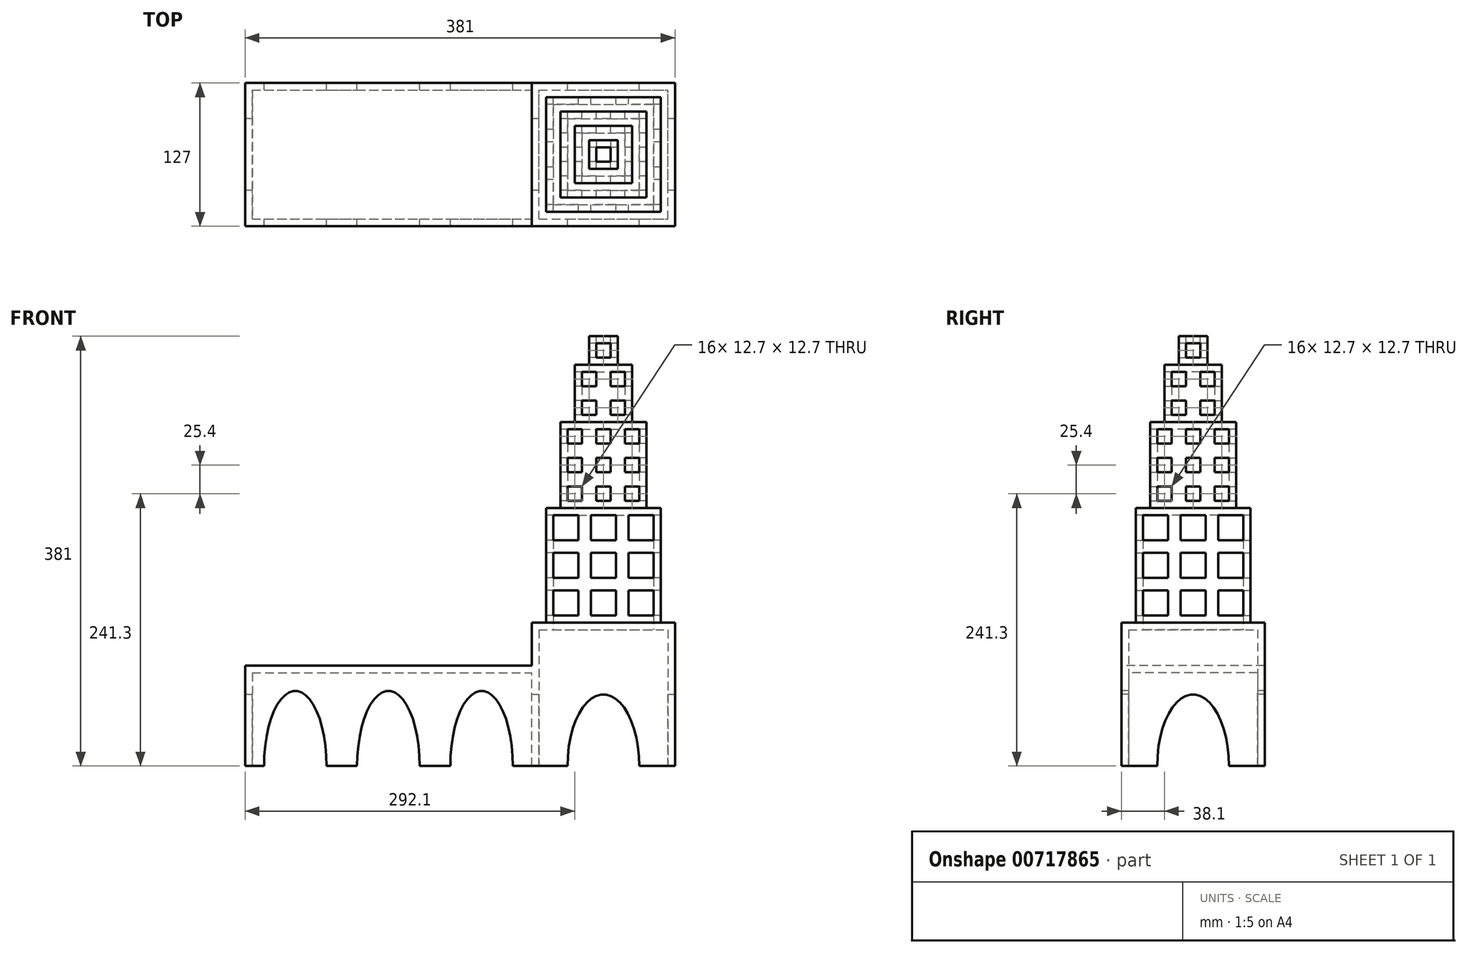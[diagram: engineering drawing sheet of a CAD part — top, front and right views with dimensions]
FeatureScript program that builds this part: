
annotation { "Feature Type Name" : "Feature", "Feature Type Description" : "" }
export const myFeature = defineFeature(function(context is Context, id is Id, definition is map)
    precondition{}
    {
        {
            var Q0;
            Q0=qCreatedBy(makeId("Front.planeOp"),FACE);
            var sketch = newSketch(context, id + "F0", { "sketchPlane" : qUnion([Q0])});
            skLineSegment(sketch, "E0.bottom", {"start": v(-63.5, 63.5) * mm, "end": v(63.5, 63.5) * mm});
            skLineSegment(sketch, "E0.top", {"start": v(-63.5, -63.5) * mm, "end": v(63.5, -63.5) * mm});
            skLineSegment(sketch, "E0.left", {"start": v(-63.5, 63.5) * mm, "end": v(-63.5, -63.5) * mm});
            skLineSegment(sketch, "E0.right", {"start": v(63.5, 63.5) * mm, "end": v(63.5, -63.5) * mm});
            skPoint(sketch, "E0.middle", {"position": v(0, 0) * mm});
            skSolve(sketch);
        }
        {
            var Q0;
            Q0 = qSketchRegion(id + "F0", true);
            extrude(context, id + "F1", {"entities" : qUnion([Q0]), "endBound" : BoundingType.SYMMETRIC, "depth" : 127 * mm, "offsetDistance" : 25.4 * mm});
        }
        {
            var Q0;
            Q0=makeQuery(id+"F1.opExtrude","SWEPT_FACE",FACE,{"disambiguationData":[OSD([sQuery(id+"F0.wireOp",EDGE,"E0.bottom")])]});
            var sketch = newSketch(context, id + "F2", { "sketchPlane" : qUnion([Q0])});
            skLineSegment(sketch, "E1.bottom", {"start": v(-50.8, 50.8) * mm, "end": v(50.8, 50.8) * mm});
            skLineSegment(sketch, "E1.top", {"start": v(-50.8, -50.8) * mm, "end": v(50.8, -50.8) * mm});
            skLineSegment(sketch, "E1.left", {"start": v(-50.8, 50.8) * mm, "end": v(-50.8, -50.8) * mm});
            skLineSegment(sketch, "E1.right", {"start": v(50.8, 50.8) * mm, "end": v(50.8, -50.8) * mm});
            skPoint(sketch, "E1.middle", {"position": v(0, 0) * mm});
            skSolve(sketch);
        }
        {
            var Q0;
            Q0 = qSketchRegion(id + "F2", true);
            extrude(context, id + "F3", {"entities" : qUnion([Q0]), "operationType" : NewBodyOperationType.ADD, "depth" : 101.6 * mm, "offsetDistance" : 25.4 * mm});
        }
        {
            var Q0;
            Q0=makeQuery(id+"F3.opExtrude","CAP_FACE",FACE,{"disambiguationData":[OSD([sQuery(id+"F2.wireOp",EDGE,"E1.bottom"),sQuery(id+"F2.wireOp",EDGE,"E1.top"),sQuery(id+"F2.wireOp",EDGE,"E1.left"),sQuery(id+"F2.wireOp",EDGE,"E1.right")])],"isStart":false});
            var sketch = newSketch(context, id + "F4", { "sketchPlane" : qUnion([Q0])});
            skLineSegment(sketch, "E2.bottom", {"start": v(-38.1, 38.1) * mm, "end": v(38.1, 38.1) * mm});
            skLineSegment(sketch, "E2.top", {"start": v(-38.1, -38.1) * mm, "end": v(38.1, -38.1) * mm});
            skLineSegment(sketch, "E2.left", {"start": v(-38.1, 38.1) * mm, "end": v(-38.1, -38.1) * mm});
            skLineSegment(sketch, "E2.right", {"start": v(38.1, 38.1) * mm, "end": v(38.1, -38.1) * mm});
            skPoint(sketch, "E2.middle", {"position": v(0, 0) * mm});
            skSolve(sketch);
        }
        {
            var Q0;
            Q0 = qSketchRegion(id + "F4", true);
            extrude(context, id + "F5", {"entities" : qUnion([Q0]), "operationType" : NewBodyOperationType.ADD, "depth" : 76.2 * mm, "offsetDistance" : 25.4 * mm});
        }
        {
            var Q0;
            Q0=makeQuery(id+"F5.opExtrude","CAP_FACE",FACE,{"disambiguationData":[OSD([sQuery(id+"F4.wireOp",EDGE,"E2.bottom"),sQuery(id+"F4.wireOp",EDGE,"E2.top"),sQuery(id+"F4.wireOp",EDGE,"E2.left"),sQuery(id+"F4.wireOp",EDGE,"E2.right")])],"isStart":false});
            var sketch = newSketch(context, id + "F6", { "sketchPlane" : qUnion([Q0])});
            skLineSegment(sketch, "E3.bottom", {"start": v(-25.4, 25.4) * mm, "end": v(25.4, 25.4) * mm});
            skLineSegment(sketch, "E3.top", {"start": v(-25.4, -25.4) * mm, "end": v(25.4, -25.4) * mm});
            skLineSegment(sketch, "E3.left", {"start": v(-25.4, 25.4) * mm, "end": v(-25.4, -25.4) * mm});
            skLineSegment(sketch, "E3.right", {"start": v(25.4, 25.4) * mm, "end": v(25.4, -25.4) * mm});
            skPoint(sketch, "E3.middle", {"position": v(0, 0) * mm});
            skSolve(sketch);
        }
        {
            var Q0;
            Q0 = qSketchRegion(id + "F6", true);
            extrude(context, id + "F7", {"entities" : qUnion([Q0]), "operationType" : NewBodyOperationType.ADD, "depth" : 50.8 * mm, "offsetDistance" : 25.4 * mm});
        }
        {
            var Q0;
            Q0=makeQuery(id+"F7.opExtrude","CAP_FACE",FACE,{"disambiguationData":[OSD([sQuery(id+"F6.wireOp",EDGE,"E3.bottom"),sQuery(id+"F6.wireOp",EDGE,"E3.top"),sQuery(id+"F6.wireOp",EDGE,"E3.left"),sQuery(id+"F6.wireOp",EDGE,"E3.right")])],"isStart":false});
            var sketch = newSketch(context, id + "F8", { "sketchPlane" : qUnion([Q0])});
            skLineSegment(sketch, "E4.bottom", {"start": v(-12.7, 12.7) * mm, "end": v(12.7, 12.7) * mm});
            skLineSegment(sketch, "E4.top", {"start": v(-12.7, -12.7) * mm, "end": v(12.7, -12.7) * mm});
            skLineSegment(sketch, "E4.left", {"start": v(-12.7, 12.7) * mm, "end": v(-12.7, -12.7) * mm});
            skLineSegment(sketch, "E4.right", {"start": v(12.7, 12.7) * mm, "end": v(12.7, -12.7) * mm});
            skPoint(sketch, "E4.middle", {"position": v(0, 0) * mm});
            skSolve(sketch);
        }
        {
            var Q0;
            Q0 = qSketchRegion(id + "F8", true);
            extrude(context, id + "F9", {"entities" : qUnion([Q0]), "operationType" : NewBodyOperationType.ADD, "depth" : 25.4 * mm, "offsetDistance" : 25.4 * mm});
        }
        {
            var Q0;
            Q0=makeQuery(id+"F1.opExtrude","SWEPT_FACE",FACE,{"disambiguationData":[OSD([sQuery(id+"F0.wireOp",EDGE,"E0.top")])]});
            shell(context, id + "F10", {"entities" : qUnion([Q0]), "thickness" : 6.35 * mm});
        }
        {
            var Q0;
            Q0=makeQuery(id+"F1.opExtrude","SWEPT_FACE",FACE,{"disambiguationData":[OSD([sQuery(id+"F0.wireOp",EDGE,"E0.left")])]});
            var sketch = newSketch(context, id + "F11", { "sketchPlane" : qUnion([Q0])});
            skLineSegment(sketch, "E5", {"start": v(63.5, -63.5) * mm, "end": v(-63.5, -63.5) * mm});
            skLineSegment(sketch, "E6", {"start": v(-63.5, -63.5) * mm, "end": v(-63.5, 25.4) * mm});
            skLineSegment(sketch, "E7", {"start": v(63.5, -63.5) * mm, "end": v(63.5, 25.4) * mm});
            skLineSegment(sketch, "E8", {"start": v(-63.5, 25.4) * mm, "end": v(63.5, 25.4) * mm});
            skSolve(sketch);
        }
        {
            var Q0;
            Q0 = qSketchRegion(id + "F11", true);
            extrude(context, id + "F12", {"entities" : qUnion([Q0]), "operationType" : NewBodyOperationType.ADD, "depth" : 254 * mm, "offsetDistance" : 25.4 * mm});
        }
        {
            var Q0;
            Q0=makeQuery(id+"F12.opExtrude","CAP_FACE",FACE,{"disambiguationData":[OSD([sQuery(id+"F11.wireOp",EDGE,"E5"),sQuery(id+"F11.wireOp",EDGE,"E6"),sQuery(id+"F11.wireOp",EDGE,"E7"),sQuery(id+"F11.wireOp",EDGE,"E8")])],"isStart":false});
            var sketch = newSketch(context, id + "F13", { "sketchPlane" : qUnion([Q0])});
            skEllipse(sketch, "E9", {"center": v(0, -63.5) * mm, "majorRadius": 63.5 * mm, "minorRadius": 31.75 * mm, "majorAxis": v(0, 1)});
            skSolve(sketch);
        }
        {
            var Q0;
            Q0=makeQuery(id+"F12.boolean.opBoolean","MERGE",FACE,{"derivedFrom":[makeQuery(id+"F1.opExtrude","SWEPT_FACE",FACE,{"disambiguationData":[OSD([sQuery(id+"F0.wireOp",EDGE,"E0.top")])]}),makeQuery(id+"F12.opExtrude","SWEPT_FACE",FACE,{"disambiguationData":[OSD([sQuery(id+"F11.wireOp",EDGE,"E5")])]})]});
            shell(context, id + "F14", {"entities" : qUnion([Q0]), "thickness" : 6.35 * mm});
        }
        {
            var Q0;
            Q0 = qSketchRegion(id + "F13", true);
            extrude(context, id + "F15", {"entities" : qUnion([Q0]), "operationType" : NewBodyOperationType.REMOVE, "endBound" : BoundingType.THROUGH_ALL, "oppositeDirection" : true, "depth" : 270 * mm, "offsetDistance" : 25.4 * mm});
        }
        {
            var Q0;
            Q0=makeQuery(id+"F12.boolean.opBoolean","MERGE",FACE,{"derivedFrom":[makeQuery(id+"F1.opExtrude","CAP_FACE",FACE,{"disambiguationData":[OSD([sQuery(id+"F0.wireOp",EDGE,"E0.bottom"),sQuery(id+"F0.wireOp",EDGE,"E0.top"),sQuery(id+"F0.wireOp",EDGE,"E0.left"),sQuery(id+"F0.wireOp",EDGE,"E0.right")])],"isStart":true}),makeQuery(id+"F12.opExtrude","SWEPT_FACE",FACE,{"disambiguationData":[OSD([sQuery(id+"F11.wireOp",EDGE,"E6")])]})]});
            var sketch = newSketch(context, id + "F16", { "sketchPlane" : qUnion([Q0])});
            skLineSegment(sketch, "E10", {"start": v(162.78, -63.5) * mm, "end": v(218.22, -63.5) * mm});
            skLineSegment(sketch, "E11", {"start": v(317.5, 3.18) * mm, "end": v(317.5, 25.4) * mm});
            skEllipticalArc(sketch, "E12", {});
            skPoint(sketch, "E13", {"position": v(190.5, 3.18) * mm});
            skPoint(sketch, "E14", {"position": v(190.5, 3.17) * mm});
            skPoint(sketch, "E15.orphan", {"position": v(63.5, -63.5) * mm});
            skPoint(sketch, "E16.orphan", {"position": v(317.5, -63.5) * mm});
            skEllipticalArc(sketch, "E17.1.0.0", {});
            skLineSegment(sketch, "E17.1.0.1", {"start": v(245.33, -63.5) * mm, "end": v(300.77, -63.5) * mm});
            skEllipticalArc(sketch, "E18.1.0.0", {});
            skLineSegment(sketch, "E19", {"start": v(80.23, -63.5) * mm, "end": v(135.67, -63.5) * mm});
            const initialGuessF16  = {"E12": [0.1905, -0.0635, 0, 1, 0.066675, 0.027722105175231253, 4.71238898038469, 1.5707963267948966], "E17.1.0.0": [0.27305, -0.0635, 0, 1, 0.066675, 0.027722105175231253, 4.71238898038469, 1.5707963267948966], "E18.1.0.0": [0.10795, -0.0635, 0, 1, 0.066675, 0.027722105175231253, 4.71238898038469, 1.5707963267948966]};
            skSetInitialGuess(sketch, initialGuessF16);
            skSolve(sketch);
        }
        {
            var Q0;
            Q0 = qSketchRegion(id + "F16", true);
            extrude(context, id + "F17", {"entities" : qUnion([Q0]), "operationType" : NewBodyOperationType.REMOVE, "oppositeDirection" : true, "depth" : 127 * mm, "offsetDistance" : 25.4 * mm});
        }
        {
            var Q0;
            Q0=makeQuery(id+"F3.opExtrude","SWEPT_FACE",FACE,{"disambiguationData":[OSD([sQuery(id+"F2.wireOp",EDGE,"E1.bottom")])]});
            var sketch = newSketch(context, id + "F18", { "sketchPlane" : qUnion([Q0])});
            skLineSegment(sketch, "E20.2", {"start": v(44.45, 158.75) * mm, "end": v(22.22, 158.75) * mm});
            skLineSegment(sketch, "E20.3", {"start": v(44.45, 136.53) * mm, "end": v(44.45, 158.75) * mm});
            skPoint(sketch, "E21.orphan", {"position": v(-44.45, 114.3) * mm});
            skPoint(sketch, "E22.orphan", {"position": v(0, 69.85) * mm});
            skPoint(sketch, "E23.orphan", {"position": v(44.45, 69.85) * mm});
            skPoint(sketch, "E24.orphan", {"position": v(-44.45, 69.85) * mm});
            skPoint(sketch, "E20.1.start.orphan", {"position": v(-44.45, 158.75) * mm});
            skLineSegment(sketch, "E25", {"start": v(22.22, 136.53) * mm, "end": v(44.45, 136.53) * mm});
            skLineSegment(sketch, "E26", {"start": v(22.22, 136.53) * mm, "end": v(22.22, 158.75) * mm});
            skPoint(sketch, "E27.orphan", {"position": v(0, 158.75) * mm});
            skPoint(sketch, "E28.start.orphan", {"position": v(0, 136.53) * mm});
            skPoint(sketch, "E29.start.orphan", {"position": v(0, 114.3) * mm});
            skPoint(sketch, "E30.orphan", {"position": v(44.45, 114.3) * mm});
            skLineSegment(sketch, "E31.0.1.0", {"start": v(22.22, 103.19) * mm, "end": v(22.22, 125.41) * mm});
            skLineSegment(sketch, "E31.0.1.1", {"start": v(44.45, 125.41) * mm, "end": v(22.22, 125.41) * mm});
            skLineSegment(sketch, "E31.0.1.2", {"start": v(44.45, 103.19) * mm, "end": v(44.45, 125.41) * mm});
            skLineSegment(sketch, "E31.0.1.3", {"start": v(22.22, 103.19) * mm, "end": v(44.45, 103.19) * mm});
            skLineSegment(sketch, "E31.0.2.0", {"start": v(22.22, 69.85) * mm, "end": v(22.22, 92.08) * mm});
            skLineSegment(sketch, "E31.0.2.1", {"start": v(44.45, 92.08) * mm, "end": v(22.22, 92.08) * mm});
            skLineSegment(sketch, "E31.0.2.2", {"start": v(44.45, 69.85) * mm, "end": v(44.45, 92.08) * mm});
            skLineSegment(sketch, "E31.0.2.3", {"start": v(22.22, 69.85) * mm, "end": v(44.45, 69.85) * mm});
            skLineSegment(sketch, "E31.1.0.0", {"start": v(-11.11, 136.53) * mm, "end": v(-11.11, 158.75) * mm});
            skLineSegment(sketch, "E31.1.0.1", {"start": v(11.11, 158.75) * mm, "end": v(-11.11, 158.75) * mm});
            skLineSegment(sketch, "E31.1.0.2", {"start": v(11.11, 136.53) * mm, "end": v(11.11, 158.75) * mm});
            skLineSegment(sketch, "E31.1.0.3", {"start": v(-11.11, 136.53) * mm, "end": v(11.11, 136.53) * mm});
            skLineSegment(sketch, "E31.1.1.0", {"start": v(-11.11, 103.19) * mm, "end": v(-11.11, 125.41) * mm});
            skLineSegment(sketch, "E31.1.1.1", {"start": v(11.11, 125.41) * mm, "end": v(-11.11, 125.41) * mm});
            skLineSegment(sketch, "E31.1.1.2", {"start": v(11.11, 103.19) * mm, "end": v(11.11, 125.41) * mm});
            skLineSegment(sketch, "E31.1.1.3", {"start": v(-11.11, 103.19) * mm, "end": v(11.11, 103.19) * mm});
            skLineSegment(sketch, "E31.1.2.0", {"start": v(-11.11, 69.85) * mm, "end": v(-11.11, 92.08) * mm});
            skLineSegment(sketch, "E31.1.2.1", {"start": v(11.11, 92.08) * mm, "end": v(-11.11, 92.08) * mm});
            skLineSegment(sketch, "E31.1.2.2", {"start": v(11.11, 69.85) * mm, "end": v(11.11, 92.08) * mm});
            skLineSegment(sketch, "E31.1.2.3", {"start": v(-11.11, 69.85) * mm, "end": v(11.11, 69.85) * mm});
            skLineSegment(sketch, "E31.2.0.0", {"start": v(-44.45, 136.53) * mm, "end": v(-44.45, 158.75) * mm});
            skLineSegment(sketch, "E31.2.0.1", {"start": v(-22.23, 158.75) * mm, "end": v(-44.45, 158.75) * mm});
            skLineSegment(sketch, "E31.2.0.2", {"start": v(-22.23, 136.53) * mm, "end": v(-22.23, 158.75) * mm});
            skLineSegment(sketch, "E31.2.0.3", {"start": v(-44.45, 136.53) * mm, "end": v(-22.23, 136.53) * mm});
            skLineSegment(sketch, "E31.2.1.0", {"start": v(-44.45, 103.19) * mm, "end": v(-44.45, 125.41) * mm});
            skLineSegment(sketch, "E31.2.1.1", {"start": v(-22.23, 125.41) * mm, "end": v(-44.45, 125.41) * mm});
            skLineSegment(sketch, "E31.2.1.2", {"start": v(-22.23, 103.19) * mm, "end": v(-22.23, 125.41) * mm});
            skLineSegment(sketch, "E31.2.1.3", {"start": v(-44.45, 103.19) * mm, "end": v(-22.23, 103.19) * mm});
            skLineSegment(sketch, "E31.2.2.0", {"start": v(-44.45, 69.85) * mm, "end": v(-44.45, 92.08) * mm});
            skLineSegment(sketch, "E31.2.2.1", {"start": v(-22.23, 92.08) * mm, "end": v(-44.45, 92.08) * mm});
            skLineSegment(sketch, "E31.2.2.2", {"start": v(-22.23, 69.85) * mm, "end": v(-22.23, 92.08) * mm});
            skLineSegment(sketch, "E31.2.2.3", {"start": v(-44.45, 69.85) * mm, "end": v(-22.23, 69.85) * mm});
            skLineSegment(sketch, "E31.direction1", {"start": v(22.22, 136.53) * mm, "end": v(-11.11, 136.53) * mm, "construction": true});
            skLineSegment(sketch, "E31.direction2", {"start": v(22.22, 136.53) * mm, "end": v(22.22, 103.19) * mm, "construction": true});
            skSolve(sketch);
        }
        {
            var Q0;
            Q0=makeQuery(id+"F18.imprint","IMPRINT",FACE,{"disambiguationData":[TD([[makeQuery(id+"F18.imprint","IMPRINT",EDGE,{"derivedFrom":sQuery(id+"F18.wireOp",EDGE,"E31.2.0.0")}),-1.0]])]});
            var Q1;
            Q1=makeQuery(id+"F18.imprint","IMPRINT",FACE,{"disambiguationData":[TD([[makeQuery(id+"F18.imprint","IMPRINT",EDGE,{"derivedFrom":sQuery(id+"F18.wireOp",EDGE,"E31.1.0.0")}),-1.0]])]});
            var Q2;
            Q2=makeQuery(id+"F18.imprint","IMPRINT",FACE,{"disambiguationData":[TD([[makeQuery(id+"F18.imprint","IMPRINT",EDGE,{"derivedFrom":sQuery(id+"F18.wireOp",EDGE,"E20.2")}),1.0]])]});
            var Q3;
            Q3=makeQuery(id+"F18.imprint","IMPRINT",FACE,{"disambiguationData":[TD([[makeQuery(id+"F18.imprint","IMPRINT",EDGE,{"derivedFrom":sQuery(id+"F18.wireOp",EDGE,"E31.0.1.0")}),-1.0]])]});
            var Q4;
            Q4=makeQuery(id+"F18.imprint","IMPRINT",FACE,{"disambiguationData":[TD([[makeQuery(id+"F18.imprint","IMPRINT",EDGE,{"derivedFrom":sQuery(id+"F18.wireOp",EDGE,"E31.1.1.0")}),-1.0]])]});
            var Q5;
            Q5=makeQuery(id+"F18.imprint","IMPRINT",FACE,{"disambiguationData":[TD([[makeQuery(id+"F18.imprint","IMPRINT",EDGE,{"derivedFrom":sQuery(id+"F18.wireOp",EDGE,"E31.2.1.0")}),-1.0]])]});
            var Q6;
            Q6=makeQuery(id+"F18.imprint","IMPRINT",FACE,{"disambiguationData":[TD([[makeQuery(id+"F18.imprint","IMPRINT",EDGE,{"derivedFrom":sQuery(id+"F18.wireOp",EDGE,"E31.2.2.0")}),-1.0]])]});
            var Q7;
            Q7=makeQuery(id+"F18.imprint","IMPRINT",FACE,{"disambiguationData":[TD([[makeQuery(id+"F18.imprint","IMPRINT",EDGE,{"derivedFrom":sQuery(id+"F18.wireOp",EDGE,"E31.1.2.0")}),-1.0]])]});
            var Q8;
            Q8=makeQuery(id+"F18.imprint","IMPRINT",FACE,{"disambiguationData":[TD([[makeQuery(id+"F18.imprint","IMPRINT",EDGE,{"derivedFrom":sQuery(id+"F18.wireOp",EDGE,"E31.0.2.0")}),-1.0]])]});
            extrude(context, id + "F19", {"entities" : qUnion([Q0, Q1, Q2, Q3, Q4, Q5, Q6, Q7, Q8]), "operationType" : NewBodyOperationType.REMOVE, "endBound" : BoundingType.THROUGH_ALL, "oppositeDirection" : true, "depth" : 25.4 * mm, "offsetDistance" : 25.4 * mm});
        }
        {
            var Q0;
            Q0=makeQuery(id+"F3.opExtrude","SWEPT_FACE",FACE,{"disambiguationData":[OSD([sQuery(id+"F2.wireOp",EDGE,"E1.left")])]});
            var sketch = newSketch(context, id + "F20", { "sketchPlane" : qUnion([Q0])});
            skLineSegment(sketch, "E32.bottom", {"start": v(22.22, 158.75) * mm, "end": v(44.45, 158.75) * mm});
            skLineSegment(sketch, "E32.top", {"start": v(22.22, 136.53) * mm, "end": v(44.45, 136.53) * mm});
            skLineSegment(sketch, "E32.left", {"start": v(22.22, 158.75) * mm, "end": v(22.22, 136.53) * mm});
            skLineSegment(sketch, "E32.right", {"start": v(44.45, 158.75) * mm, "end": v(44.45, 136.53) * mm});
            skPoint(sketch, "E32.middle", {"position": v(33.34, 147.64) * mm});
            skLineSegment(sketch, "E33.0.1.0", {"start": v(22.22, 125.41) * mm, "end": v(22.22, 103.19) * mm});
            skLineSegment(sketch, "E33.0.1.1", {"start": v(22.22, 103.19) * mm, "end": v(44.45, 103.19) * mm});
            skLineSegment(sketch, "E33.0.1.2", {"start": v(44.45, 125.41) * mm, "end": v(44.45, 103.19) * mm});
            skLineSegment(sketch, "E33.0.1.3", {"start": v(22.22, 125.41) * mm, "end": v(44.45, 125.41) * mm});
            skLineSegment(sketch, "E33.0.2.0", {"start": v(22.22, 92.08) * mm, "end": v(22.22, 69.85) * mm});
            skLineSegment(sketch, "E33.0.2.1", {"start": v(22.22, 69.85) * mm, "end": v(44.45, 69.85) * mm});
            skLineSegment(sketch, "E33.0.2.2", {"start": v(44.45, 92.08) * mm, "end": v(44.45, 69.85) * mm});
            skLineSegment(sketch, "E33.0.2.3", {"start": v(22.22, 92.08) * mm, "end": v(44.45, 92.08) * mm});
            skLineSegment(sketch, "E33.1.0.0", {"start": v(-11.11, 158.75) * mm, "end": v(-11.11, 136.53) * mm});
            skLineSegment(sketch, "E33.1.0.1", {"start": v(-11.11, 136.53) * mm, "end": v(11.11, 136.53) * mm});
            skLineSegment(sketch, "E33.1.0.2", {"start": v(11.11, 158.75) * mm, "end": v(11.11, 136.53) * mm});
            skLineSegment(sketch, "E33.1.0.3", {"start": v(-11.11, 158.75) * mm, "end": v(11.11, 158.75) * mm});
            skLineSegment(sketch, "E33.1.1.0", {"start": v(-11.11, 125.41) * mm, "end": v(-11.11, 103.19) * mm});
            skLineSegment(sketch, "E33.1.1.1", {"start": v(-11.11, 103.19) * mm, "end": v(11.11, 103.19) * mm});
            skLineSegment(sketch, "E33.1.1.2", {"start": v(11.11, 125.41) * mm, "end": v(11.11, 103.19) * mm});
            skLineSegment(sketch, "E33.1.1.3", {"start": v(-11.11, 125.41) * mm, "end": v(11.11, 125.41) * mm});
            skLineSegment(sketch, "E33.1.2.0", {"start": v(-11.11, 92.08) * mm, "end": v(-11.11, 69.85) * mm});
            skLineSegment(sketch, "E33.1.2.1", {"start": v(-11.11, 69.85) * mm, "end": v(11.11, 69.85) * mm});
            skLineSegment(sketch, "E33.1.2.2", {"start": v(11.11, 92.08) * mm, "end": v(11.11, 69.85) * mm});
            skLineSegment(sketch, "E33.1.2.3", {"start": v(-11.11, 92.08) * mm, "end": v(11.11, 92.08) * mm});
            skLineSegment(sketch, "E33.2.0.0", {"start": v(-44.45, 158.75) * mm, "end": v(-44.45, 136.53) * mm});
            skLineSegment(sketch, "E33.2.0.1", {"start": v(-44.45, 136.53) * mm, "end": v(-22.23, 136.53) * mm});
            skLineSegment(sketch, "E33.2.0.2", {"start": v(-22.23, 158.75) * mm, "end": v(-22.23, 136.53) * mm});
            skLineSegment(sketch, "E33.2.0.3", {"start": v(-44.45, 158.75) * mm, "end": v(-22.23, 158.75) * mm});
            skLineSegment(sketch, "E33.2.1.0", {"start": v(-44.45, 125.41) * mm, "end": v(-44.45, 103.19) * mm});
            skLineSegment(sketch, "E33.2.1.1", {"start": v(-44.45, 103.19) * mm, "end": v(-22.23, 103.19) * mm});
            skLineSegment(sketch, "E33.2.1.2", {"start": v(-22.23, 125.41) * mm, "end": v(-22.23, 103.19) * mm});
            skLineSegment(sketch, "E33.2.1.3", {"start": v(-44.45, 125.41) * mm, "end": v(-22.23, 125.41) * mm});
            skLineSegment(sketch, "E33.2.2.0", {"start": v(-44.45, 92.08) * mm, "end": v(-44.45, 69.85) * mm});
            skLineSegment(sketch, "E33.2.2.1", {"start": v(-44.45, 69.85) * mm, "end": v(-22.23, 69.85) * mm});
            skLineSegment(sketch, "E33.2.2.2", {"start": v(-22.23, 92.08) * mm, "end": v(-22.23, 69.85) * mm});
            skLineSegment(sketch, "E33.2.2.3", {"start": v(-44.45, 92.08) * mm, "end": v(-22.23, 92.08) * mm});
            skLineSegment(sketch, "E33.direction1", {"start": v(22.22, 136.53) * mm, "end": v(-11.11, 136.53) * mm, "construction": true});
            skLineSegment(sketch, "E33.direction2", {"start": v(22.22, 136.53) * mm, "end": v(22.22, 103.19) * mm, "construction": true});
            skSolve(sketch);
        }
        {
            var Q0;
            Q0=makeQuery(id+"F20.imprint","IMPRINT",FACE,{"disambiguationData":[TD([[makeQuery(id+"F20.imprint","IMPRINT",EDGE,{"derivedFrom":sQuery(id+"F20.wireOp",EDGE,"E33.2.0.0")}),1.0]])]});
            var Q1;
            Q1=makeQuery(id+"F20.imprint","IMPRINT",FACE,{"disambiguationData":[TD([[makeQuery(id+"F20.imprint","IMPRINT",EDGE,{"derivedFrom":sQuery(id+"F20.wireOp",EDGE,"E33.1.0.0")}),1.0]])]});
            var Q2;
            Q2=makeQuery(id+"F20.imprint","IMPRINT",FACE,{"disambiguationData":[TD([[makeQuery(id+"F20.imprint","IMPRINT",EDGE,{"derivedFrom":sQuery(id+"F20.wireOp",EDGE,"E32.bottom")}),-1.0]])]});
            var Q3;
            Q3=makeQuery(id+"F20.imprint","IMPRINT",FACE,{"disambiguationData":[TD([[makeQuery(id+"F20.imprint","IMPRINT",EDGE,{"derivedFrom":sQuery(id+"F20.wireOp",EDGE,"E33.2.1.0")}),1.0]])]});
            var Q4;
            Q4=makeQuery(id+"F20.imprint","IMPRINT",FACE,{"disambiguationData":[TD([[makeQuery(id+"F20.imprint","IMPRINT",EDGE,{"derivedFrom":sQuery(id+"F20.wireOp",EDGE,"E33.1.1.0")}),1.0]])]});
            var Q5;
            Q5=makeQuery(id+"F20.imprint","IMPRINT",FACE,{"disambiguationData":[TD([[makeQuery(id+"F20.imprint","IMPRINT",EDGE,{"derivedFrom":sQuery(id+"F20.wireOp",EDGE,"E33.0.1.0")}),1.0]])]});
            var Q6;
            Q6=makeQuery(id+"F20.imprint","IMPRINT",FACE,{"disambiguationData":[TD([[makeQuery(id+"F20.imprint","IMPRINT",EDGE,{"derivedFrom":sQuery(id+"F20.wireOp",EDGE,"E33.2.2.0")}),1.0]])]});
            var Q7;
            Q7=makeQuery(id+"F20.imprint","IMPRINT",FACE,{"disambiguationData":[TD([[makeQuery(id+"F20.imprint","IMPRINT",EDGE,{"derivedFrom":sQuery(id+"F20.wireOp",EDGE,"E33.1.2.0")}),1.0]])]});
            var Q8;
            Q8=makeQuery(id+"F20.imprint","IMPRINT",FACE,{"disambiguationData":[TD([[makeQuery(id+"F20.imprint","IMPRINT",EDGE,{"derivedFrom":sQuery(id+"F20.wireOp",EDGE,"E33.0.2.0")}),1.0]])]});
            extrude(context, id + "F21", {"entities" : qUnion([Q0, Q1, Q2, Q3, Q4, Q5, Q6, Q7, Q8]), "operationType" : NewBodyOperationType.REMOVE, "endBound" : BoundingType.THROUGH_ALL, "oppositeDirection" : true, "depth" : 25.4 * mm, "offsetDistance" : 25.4 * mm});
        }
        {
            var Q0;
            Q0=makeQuery(id+"F9.opExtrude","SWEPT_FACE",FACE,{"disambiguationData":[OSD([sQuery(id+"F8.wireOp",EDGE,"E4.bottom")])]});
            var sketch = newSketch(context, id + "F22", { "sketchPlane" : qUnion([Q0])});
            skLineSegment(sketch, "E34.0", {"start": v(6.35, 311.15) * mm, "end": v(-6.35, 311.15) * mm});
            skLineSegment(sketch, "E34.1", {"start": v(6.35, 311.15) * mm, "end": v(6.35, 298.45) * mm});
            skLineSegment(sketch, "E34.2", {"start": v(6.35, 298.45) * mm, "end": v(-6.35, 298.45) * mm});
            skLineSegment(sketch, "E34.3", {"start": v(-6.35, 311.15) * mm, "end": v(-6.35, 298.45) * mm});
            skSolve(sketch);
        }
        {
            var Q0;
            Q0=makeQuery(id+"F22.imprint","IMPRINT",FACE,{"disambiguationData":[TD([[makeQuery(id+"F22.imprint","IMPRINT",EDGE,{"derivedFrom":sQuery(id+"F22.wireOp",EDGE,"E34.0")}),1.0]])]});
            extrude(context, id + "F23", {"entities" : qUnion([Q0]), "operationType" : NewBodyOperationType.REMOVE, "endBound" : BoundingType.THROUGH_ALL, "oppositeDirection" : true, "depth" : 25.4 * mm, "offsetDistance" : 25.4 * mm});
        }
        {
            var Q0;
            Q0=makeQuery(id+"F9.opExtrude","SWEPT_FACE",FACE,{"disambiguationData":[OSD([sQuery(id+"F8.wireOp",EDGE,"E4.left")])]});
            var sketch = newSketch(context, id + "F24", { "sketchPlane" : qUnion([Q0])});
            skLineSegment(sketch, "E35.0", {"start": v(-6.35, 311.15) * mm, "end": v(-6.35, 298.45) * mm});
            skLineSegment(sketch, "E35.1", {"start": v(-6.35, 311.15) * mm, "end": v(6.35, 311.15) * mm});
            skLineSegment(sketch, "E35.2", {"start": v(6.35, 311.15) * mm, "end": v(6.35, 298.45) * mm});
            skLineSegment(sketch, "E35.3", {"start": v(-6.35, 298.45) * mm, "end": v(6.35, 298.45) * mm});
            skSolve(sketch);
        }
        {
            var Q0;
            Q0=makeQuery(id+"F24.imprint","IMPRINT",FACE,{"disambiguationData":[TD([[makeQuery(id+"F24.imprint","IMPRINT",EDGE,{"derivedFrom":sQuery(id+"F24.wireOp",EDGE,"E35.0")}),1.0]])]});
            extrude(context, id + "F25", {"entities" : qUnion([Q0]), "operationType" : NewBodyOperationType.REMOVE, "endBound" : BoundingType.THROUGH_ALL, "oppositeDirection" : true, "depth" : 25.4 * mm, "offsetDistance" : 25.4 * mm});
        }
        {
            var Q0;
            Q0=makeQuery(id+"F12.boolean.opBoolean","MERGE",FACE,{"derivedFrom":[makeQuery(id+"F1.opExtrude","CAP_FACE",FACE,{"disambiguationData":[OSD([sQuery(id+"F0.wireOp",EDGE,"E0.bottom"),sQuery(id+"F0.wireOp",EDGE,"E0.top"),sQuery(id+"F0.wireOp",EDGE,"E0.left"),sQuery(id+"F0.wireOp",EDGE,"E0.right")])],"isStart":true}),makeQuery(id+"F12.opExtrude","SWEPT_FACE",FACE,{"disambiguationData":[OSD([sQuery(id+"F11.wireOp",EDGE,"E6")])]})]});
            var sketch = newSketch(context, id + "F26", { "sketchPlane" : qUnion([Q0])});
            skEllipse(sketch, "E36", {"center": v(0, -63.5) * mm, "majorRadius": 63.5 * mm, "minorRadius": 31.75 * mm, "majorAxis": v(0, 1)});
            skSolve(sketch);
        }
        {
            var Q0;
            Q0 = qSketchRegion(id + "F26", true);
            extrude(context, id + "F27", {"entities" : qUnion([Q0]), "operationType" : NewBodyOperationType.REMOVE, "endBound" : BoundingType.THROUGH_ALL, "oppositeDirection" : true, "depth" : 25.4 * mm, "offsetDistance" : 25.4 * mm});
        }
        {
            var Q0;
            Q0=makeQuery(id+"F5.opExtrude","SWEPT_FACE",FACE,{"disambiguationData":[OSD([sQuery(id+"F4.wireOp",EDGE,"E2.bottom")])]});
            var sketch = newSketch(context, id + "F28", { "sketchPlane" : qUnion([Q0])});
            skLineSegment(sketch, "E37.bottom", {"start": v(19.05, 234.95) * mm, "end": v(31.75, 234.95) * mm});
            skLineSegment(sketch, "E37.top", {"start": v(19.05, 222.25) * mm, "end": v(31.75, 222.25) * mm});
            skLineSegment(sketch, "E37.left", {"start": v(19.05, 234.95) * mm, "end": v(19.05, 222.25) * mm});
            skLineSegment(sketch, "E37.right", {"start": v(31.75, 234.95) * mm, "end": v(31.75, 222.25) * mm});
            skPoint(sketch, "E37.middle", {"position": v(25.4, 228.6) * mm});
            skLineSegment(sketch, "E38.0.1.0", {"start": v(19.05, 209.55) * mm, "end": v(31.75, 209.55) * mm});
            skLineSegment(sketch, "E38.0.1.1", {"start": v(19.05, 209.55) * mm, "end": v(19.05, 196.85) * mm});
            skLineSegment(sketch, "E38.0.1.2", {"start": v(19.05, 196.85) * mm, "end": v(31.75, 196.85) * mm});
            skLineSegment(sketch, "E38.0.1.3", {"start": v(31.75, 209.55) * mm, "end": v(31.75, 196.85) * mm});
            skLineSegment(sketch, "E38.0.2.0", {"start": v(19.05, 184.15) * mm, "end": v(31.75, 184.15) * mm});
            skLineSegment(sketch, "E38.0.2.1", {"start": v(19.05, 184.15) * mm, "end": v(19.05, 171.45) * mm});
            skLineSegment(sketch, "E38.0.2.2", {"start": v(19.05, 171.45) * mm, "end": v(31.75, 171.45) * mm});
            skLineSegment(sketch, "E38.0.2.3", {"start": v(31.75, 184.15) * mm, "end": v(31.75, 171.45) * mm});
            skLineSegment(sketch, "E38.1.0.0", {"start": v(-6.35, 234.95) * mm, "end": v(6.35, 234.95) * mm});
            skLineSegment(sketch, "E38.1.0.1", {"start": v(-6.35, 234.95) * mm, "end": v(-6.35, 222.25) * mm});
            skLineSegment(sketch, "E38.1.0.2", {"start": v(-6.35, 222.25) * mm, "end": v(6.35, 222.25) * mm});
            skLineSegment(sketch, "E38.1.0.3", {"start": v(6.35, 234.95) * mm, "end": v(6.35, 222.25) * mm});
            skLineSegment(sketch, "E38.1.1.0", {"start": v(-6.35, 209.55) * mm, "end": v(6.35, 209.55) * mm});
            skLineSegment(sketch, "E38.1.1.1", {"start": v(-6.35, 209.55) * mm, "end": v(-6.35, 196.85) * mm});
            skLineSegment(sketch, "E38.1.1.2", {"start": v(-6.35, 196.85) * mm, "end": v(6.35, 196.85) * mm});
            skLineSegment(sketch, "E38.1.1.3", {"start": v(6.35, 209.55) * mm, "end": v(6.35, 196.85) * mm});
            skLineSegment(sketch, "E38.1.2.0", {"start": v(-6.35, 184.15) * mm, "end": v(6.35, 184.15) * mm});
            skLineSegment(sketch, "E38.1.2.1", {"start": v(-6.35, 184.15) * mm, "end": v(-6.35, 171.45) * mm});
            skLineSegment(sketch, "E38.1.2.2", {"start": v(-6.35, 171.45) * mm, "end": v(6.35, 171.45) * mm});
            skLineSegment(sketch, "E38.1.2.3", {"start": v(6.35, 184.15) * mm, "end": v(6.35, 171.45) * mm});
            skLineSegment(sketch, "E38.2.0.0", {"start": v(-31.75, 234.95) * mm, "end": v(-19.05, 234.95) * mm});
            skLineSegment(sketch, "E38.2.0.1", {"start": v(-31.75, 234.95) * mm, "end": v(-31.75, 222.25) * mm});
            skLineSegment(sketch, "E38.2.0.2", {"start": v(-31.75, 222.25) * mm, "end": v(-19.05, 222.25) * mm});
            skLineSegment(sketch, "E38.2.0.3", {"start": v(-19.05, 234.95) * mm, "end": v(-19.05, 222.25) * mm});
            skLineSegment(sketch, "E38.2.1.0", {"start": v(-31.75, 209.55) * mm, "end": v(-19.05, 209.55) * mm});
            skLineSegment(sketch, "E38.2.1.1", {"start": v(-31.75, 209.55) * mm, "end": v(-31.75, 196.85) * mm});
            skLineSegment(sketch, "E38.2.1.2", {"start": v(-31.75, 196.85) * mm, "end": v(-19.05, 196.85) * mm});
            skLineSegment(sketch, "E38.2.1.3", {"start": v(-19.05, 209.55) * mm, "end": v(-19.05, 196.85) * mm});
            skLineSegment(sketch, "E38.2.2.0", {"start": v(-31.75, 184.15) * mm, "end": v(-19.05, 184.15) * mm});
            skLineSegment(sketch, "E38.2.2.1", {"start": v(-31.75, 184.15) * mm, "end": v(-31.75, 171.45) * mm});
            skLineSegment(sketch, "E38.2.2.2", {"start": v(-31.75, 171.45) * mm, "end": v(-19.05, 171.45) * mm});
            skLineSegment(sketch, "E38.2.2.3", {"start": v(-19.05, 184.15) * mm, "end": v(-19.05, 171.45) * mm});
            skLineSegment(sketch, "E38.direction1", {"start": v(19.05, 234.95) * mm, "end": v(-6.35, 234.95) * mm, "construction": true});
            skLineSegment(sketch, "E38.direction2", {"start": v(19.05, 234.95) * mm, "end": v(19.05, 209.55) * mm, "construction": true});
            skSolve(sketch);
        }
        {
            var Q0;
            Q0=makeQuery(id+"F28.imprint","IMPRINT",FACE,{"disambiguationData":[TD([[makeQuery(id+"F28.imprint","IMPRINT",EDGE,{"derivedFrom":sQuery(id+"F28.wireOp",EDGE,"E38.2.0.0")}),-1.0]])]});
            var Q1;
            Q1=makeQuery(id+"F28.imprint","IMPRINT",FACE,{"disambiguationData":[TD([[makeQuery(id+"F28.imprint","IMPRINT",EDGE,{"derivedFrom":sQuery(id+"F28.wireOp",EDGE,"E38.2.1.0")}),-1.0]])]});
            var Q2;
            Q2=makeQuery(id+"F28.imprint","IMPRINT",FACE,{"disambiguationData":[TD([[makeQuery(id+"F28.imprint","IMPRINT",EDGE,{"derivedFrom":sQuery(id+"F28.wireOp",EDGE,"E38.2.2.0")}),-1.0]])]});
            var Q3;
            Q3=makeQuery(id+"F28.imprint","IMPRINT",FACE,{"disambiguationData":[TD([[makeQuery(id+"F28.imprint","IMPRINT",EDGE,{"derivedFrom":sQuery(id+"F28.wireOp",EDGE,"E38.1.2.0")}),-1.0]])]});
            var Q4;
            Q4=makeQuery(id+"F28.imprint","IMPRINT",FACE,{"disambiguationData":[TD([[makeQuery(id+"F28.imprint","IMPRINT",EDGE,{"derivedFrom":sQuery(id+"F28.wireOp",EDGE,"E38.1.1.0")}),-1.0]])]});
            var Q5;
            Q5=makeQuery(id+"F28.imprint","IMPRINT",FACE,{"disambiguationData":[TD([[makeQuery(id+"F28.imprint","IMPRINT",EDGE,{"derivedFrom":sQuery(id+"F28.wireOp",EDGE,"E38.1.0.0")}),-1.0]])]});
            var Q6;
            Q6=makeQuery(id+"F28.imprint","IMPRINT",FACE,{"disambiguationData":[TD([[makeQuery(id+"F28.imprint","IMPRINT",EDGE,{"derivedFrom":sQuery(id+"F28.wireOp",EDGE,"E37.bottom")}),-1.0]])]});
            var Q7;
            Q7=makeQuery(id+"F28.imprint","IMPRINT",FACE,{"disambiguationData":[TD([[makeQuery(id+"F28.imprint","IMPRINT",EDGE,{"derivedFrom":sQuery(id+"F28.wireOp",EDGE,"E38.0.1.0")}),-1.0]])]});
            var Q8;
            Q8=makeQuery(id+"F28.imprint","IMPRINT",FACE,{"disambiguationData":[TD([[makeQuery(id+"F28.imprint","IMPRINT",EDGE,{"derivedFrom":sQuery(id+"F28.wireOp",EDGE,"E38.0.2.0")}),-1.0]])]});
            extrude(context, id + "F29", {"entities" : qUnion([Q0, Q1, Q2, Q3, Q4, Q5, Q6, Q7, Q8]), "operationType" : NewBodyOperationType.REMOVE, "endBound" : BoundingType.THROUGH_ALL, "oppositeDirection" : true, "depth" : 25.4 * mm, "offsetDistance" : 25.4 * mm});
        }
        {
            var Q0;
            Q0=makeQuery(id+"F5.opExtrude","SWEPT_FACE",FACE,{"disambiguationData":[OSD([sQuery(id+"F4.wireOp",EDGE,"E2.left")])]});
            var sketch = newSketch(context, id + "F30", { "sketchPlane" : qUnion([Q0])});
            skLineSegment(sketch, "E39.bottom", {"start": v(19.05, 234.95) * mm, "end": v(31.75, 234.95) * mm});
            skLineSegment(sketch, "E39.top", {"start": v(19.05, 222.25) * mm, "end": v(31.75, 222.25) * mm});
            skLineSegment(sketch, "E39.left", {"start": v(19.05, 234.95) * mm, "end": v(19.05, 222.25) * mm});
            skLineSegment(sketch, "E39.right", {"start": v(31.75, 234.95) * mm, "end": v(31.75, 222.25) * mm});
            skPoint(sketch, "E39.middle", {"position": v(25.4, 228.6) * mm});
            skLineSegment(sketch, "E40.0.1.0", {"start": v(19.05, 209.55) * mm, "end": v(31.75, 209.55) * mm});
            skLineSegment(sketch, "E40.0.1.1", {"start": v(19.05, 209.55) * mm, "end": v(19.05, 196.85) * mm});
            skLineSegment(sketch, "E40.0.1.2", {"start": v(19.05, 196.85) * mm, "end": v(31.75, 196.85) * mm});
            skLineSegment(sketch, "E40.0.1.3", {"start": v(31.75, 209.55) * mm, "end": v(31.75, 196.85) * mm});
            skLineSegment(sketch, "E40.0.2.0", {"start": v(19.05, 184.15) * mm, "end": v(31.75, 184.15) * mm});
            skLineSegment(sketch, "E40.0.2.1", {"start": v(19.05, 184.15) * mm, "end": v(19.05, 171.45) * mm});
            skLineSegment(sketch, "E40.0.2.2", {"start": v(19.05, 171.45) * mm, "end": v(31.75, 171.45) * mm});
            skLineSegment(sketch, "E40.0.2.3", {"start": v(31.75, 184.15) * mm, "end": v(31.75, 171.45) * mm});
            skLineSegment(sketch, "E40.1.0.0", {"start": v(-6.35, 234.95) * mm, "end": v(6.35, 234.95) * mm});
            skLineSegment(sketch, "E40.1.0.1", {"start": v(-6.35, 234.95) * mm, "end": v(-6.35, 222.25) * mm});
            skLineSegment(sketch, "E40.1.0.2", {"start": v(-6.35, 222.25) * mm, "end": v(6.35, 222.25) * mm});
            skLineSegment(sketch, "E40.1.0.3", {"start": v(6.35, 234.95) * mm, "end": v(6.35, 222.25) * mm});
            skLineSegment(sketch, "E40.1.1.0", {"start": v(-6.35, 209.55) * mm, "end": v(6.35, 209.55) * mm});
            skLineSegment(sketch, "E40.1.1.1", {"start": v(-6.35, 209.55) * mm, "end": v(-6.35, 196.85) * mm});
            skLineSegment(sketch, "E40.1.1.2", {"start": v(-6.35, 196.85) * mm, "end": v(6.35, 196.85) * mm});
            skLineSegment(sketch, "E40.1.1.3", {"start": v(6.35, 209.55) * mm, "end": v(6.35, 196.85) * mm});
            skLineSegment(sketch, "E40.1.2.0", {"start": v(-6.35, 184.15) * mm, "end": v(6.35, 184.15) * mm});
            skLineSegment(sketch, "E40.1.2.1", {"start": v(-6.35, 184.15) * mm, "end": v(-6.35, 171.45) * mm});
            skLineSegment(sketch, "E40.1.2.2", {"start": v(-6.35, 171.45) * mm, "end": v(6.35, 171.45) * mm});
            skLineSegment(sketch, "E40.1.2.3", {"start": v(6.35, 184.15) * mm, "end": v(6.35, 171.45) * mm});
            skLineSegment(sketch, "E40.2.0.0", {"start": v(-31.75, 234.95) * mm, "end": v(-19.05, 234.95) * mm});
            skLineSegment(sketch, "E40.2.0.1", {"start": v(-31.75, 234.95) * mm, "end": v(-31.75, 222.25) * mm});
            skLineSegment(sketch, "E40.2.0.2", {"start": v(-31.75, 222.25) * mm, "end": v(-19.05, 222.25) * mm});
            skLineSegment(sketch, "E40.2.0.3", {"start": v(-19.05, 234.95) * mm, "end": v(-19.05, 222.25) * mm});
            skLineSegment(sketch, "E40.2.1.0", {"start": v(-31.75, 209.55) * mm, "end": v(-19.05, 209.55) * mm});
            skLineSegment(sketch, "E40.2.1.1", {"start": v(-31.75, 209.55) * mm, "end": v(-31.75, 196.85) * mm});
            skLineSegment(sketch, "E40.2.1.2", {"start": v(-31.75, 196.85) * mm, "end": v(-19.05, 196.85) * mm});
            skLineSegment(sketch, "E40.2.1.3", {"start": v(-19.05, 209.55) * mm, "end": v(-19.05, 196.85) * mm});
            skLineSegment(sketch, "E40.2.2.0", {"start": v(-31.75, 184.15) * mm, "end": v(-19.05, 184.15) * mm});
            skLineSegment(sketch, "E40.2.2.1", {"start": v(-31.75, 184.15) * mm, "end": v(-31.75, 171.45) * mm});
            skLineSegment(sketch, "E40.2.2.2", {"start": v(-31.75, 171.45) * mm, "end": v(-19.05, 171.45) * mm});
            skLineSegment(sketch, "E40.2.2.3", {"start": v(-19.05, 184.15) * mm, "end": v(-19.05, 171.45) * mm});
            skLineSegment(sketch, "E40.direction1", {"start": v(19.05, 234.95) * mm, "end": v(-6.35, 234.95) * mm, "construction": true});
            skLineSegment(sketch, "E40.direction2", {"start": v(19.05, 234.95) * mm, "end": v(19.05, 209.55) * mm, "construction": true});
            skSolve(sketch);
        }
        {
            var Q0;
            Q0=makeQuery(id+"F30.imprint","IMPRINT",FACE,{"disambiguationData":[TD([[makeQuery(id+"F30.imprint","IMPRINT",EDGE,{"derivedFrom":sQuery(id+"F30.wireOp",EDGE,"E40.2.0.0")}),-1.0]])]});
            var Q1;
            Q1=makeQuery(id+"F30.imprint","IMPRINT",FACE,{"disambiguationData":[TD([[makeQuery(id+"F30.imprint","IMPRINT",EDGE,{"derivedFrom":sQuery(id+"F30.wireOp",EDGE,"E40.1.0.0")}),-1.0]])]});
            var Q2;
            Q2=makeQuery(id+"F30.imprint","IMPRINT",FACE,{"disambiguationData":[TD([[makeQuery(id+"F30.imprint","IMPRINT",EDGE,{"derivedFrom":sQuery(id+"F30.wireOp",EDGE,"E39.bottom")}),-1.0]])]});
            var Q3;
            Q3=makeQuery(id+"F30.imprint","IMPRINT",FACE,{"disambiguationData":[TD([[makeQuery(id+"F30.imprint","IMPRINT",EDGE,{"derivedFrom":sQuery(id+"F30.wireOp",EDGE,"E40.0.1.0")}),-1.0]])]});
            var Q4;
            Q4=makeQuery(id+"F30.imprint","IMPRINT",FACE,{"disambiguationData":[TD([[makeQuery(id+"F30.imprint","IMPRINT",EDGE,{"derivedFrom":sQuery(id+"F30.wireOp",EDGE,"E40.1.1.0")}),-1.0]])]});
            var Q5;
            Q5=makeQuery(id+"F30.imprint","IMPRINT",FACE,{"disambiguationData":[TD([[makeQuery(id+"F30.imprint","IMPRINT",EDGE,{"derivedFrom":sQuery(id+"F30.wireOp",EDGE,"E40.1.2.0")}),-1.0]])]});
            var Q6;
            Q6=makeQuery(id+"F30.imprint","IMPRINT",FACE,{"disambiguationData":[TD([[makeQuery(id+"F30.imprint","IMPRINT",EDGE,{"derivedFrom":sQuery(id+"F30.wireOp",EDGE,"E40.2.2.0")}),-1.0]])]});
            var Q7;
            Q7=makeQuery(id+"F30.imprint","IMPRINT",FACE,{"disambiguationData":[TD([[makeQuery(id+"F30.imprint","IMPRINT",EDGE,{"derivedFrom":sQuery(id+"F30.wireOp",EDGE,"E40.2.1.0")}),-1.0]])]});
            var Q8;
            Q8=makeQuery(id+"F30.imprint","IMPRINT",FACE,{"disambiguationData":[TD([[makeQuery(id+"F30.imprint","IMPRINT",EDGE,{"derivedFrom":sQuery(id+"F30.wireOp",EDGE,"E40.0.2.0")}),-1.0]])]});
            extrude(context, id + "F31", {"entities" : qUnion([Q0, Q1, Q2, Q3, Q4, Q5, Q6, Q7, Q8]), "operationType" : NewBodyOperationType.REMOVE, "endBound" : BoundingType.THROUGH_ALL, "oppositeDirection" : true, "depth" : 25.4 * mm, "offsetDistance" : 25.4 * mm});
        }
        {
            var Q0;
            Q0=makeQuery(id+"F7.opExtrude","SWEPT_FACE",FACE,{"disambiguationData":[OSD([sQuery(id+"F6.wireOp",EDGE,"E3.bottom")])]});
            var sketch = newSketch(context, id + "F32", { "sketchPlane" : qUnion([Q0])});
            skLineSegment(sketch, "E41.bottom", {"start": v(6.35, 285.75) * mm, "end": v(19.05, 285.75) * mm});
            skLineSegment(sketch, "E41.top", {"start": v(6.35, 273.05) * mm, "end": v(19.05, 273.05) * mm});
            skLineSegment(sketch, "E41.left", {"start": v(6.35, 285.75) * mm, "end": v(6.35, 273.05) * mm});
            skLineSegment(sketch, "E41.right", {"start": v(19.05, 285.75) * mm, "end": v(19.05, 273.05) * mm});
            skPoint(sketch, "E41.middle", {"position": v(12.7, 279.4) * mm});
            skLineSegment(sketch, "E42.0.1.0", {"start": v(6.35, 260.35) * mm, "end": v(19.05, 260.35) * mm});
            skLineSegment(sketch, "E42.0.1.1", {"start": v(6.35, 260.35) * mm, "end": v(6.35, 247.65) * mm});
            skLineSegment(sketch, "E42.0.1.2", {"start": v(6.35, 247.65) * mm, "end": v(19.05, 247.65) * mm});
            skLineSegment(sketch, "E42.0.1.3", {"start": v(19.05, 260.35) * mm, "end": v(19.05, 247.65) * mm});
            skLineSegment(sketch, "E42.1.0.0", {"start": v(-19.05, 285.75) * mm, "end": v(-6.35, 285.75) * mm});
            skLineSegment(sketch, "E42.1.0.1", {"start": v(-19.05, 285.75) * mm, "end": v(-19.05, 273.05) * mm});
            skLineSegment(sketch, "E42.1.0.2", {"start": v(-19.05, 273.05) * mm, "end": v(-6.35, 273.05) * mm});
            skLineSegment(sketch, "E42.1.0.3", {"start": v(-6.35, 285.75) * mm, "end": v(-6.35, 273.05) * mm});
            skLineSegment(sketch, "E42.1.1.0", {"start": v(-19.05, 260.35) * mm, "end": v(-6.35, 260.35) * mm});
            skLineSegment(sketch, "E42.1.1.1", {"start": v(-19.05, 260.35) * mm, "end": v(-19.05, 247.65) * mm});
            skLineSegment(sketch, "E42.1.1.2", {"start": v(-19.05, 247.65) * mm, "end": v(-6.35, 247.65) * mm});
            skLineSegment(sketch, "E42.1.1.3", {"start": v(-6.35, 260.35) * mm, "end": v(-6.35, 247.65) * mm});
            skLineSegment(sketch, "E42.direction1", {"start": v(6.35, 285.75) * mm, "end": v(-19.05, 285.75) * mm, "construction": true});
            skLineSegment(sketch, "E42.direction2", {"start": v(6.35, 285.75) * mm, "end": v(6.35, 260.35) * mm, "construction": true});
            skSolve(sketch);
        }
        {
            var Q0;
            Q0=makeQuery(id+"F32.imprint","IMPRINT",FACE,{"disambiguationData":[TD([[makeQuery(id+"F32.imprint","IMPRINT",EDGE,{"derivedFrom":sQuery(id+"F32.wireOp",EDGE,"E42.1.0.0")}),-1.0]])]});
            var Q1;
            Q1=makeQuery(id+"F32.imprint","IMPRINT",FACE,{"disambiguationData":[TD([[makeQuery(id+"F32.imprint","IMPRINT",EDGE,{"derivedFrom":sQuery(id+"F32.wireOp",EDGE,"E42.1.1.0")}),-1.0]])]});
            var Q2;
            Q2=makeQuery(id+"F32.imprint","IMPRINT",FACE,{"disambiguationData":[TD([[makeQuery(id+"F32.imprint","IMPRINT",EDGE,{"derivedFrom":sQuery(id+"F32.wireOp",EDGE,"E42.0.1.0")}),-1.0]])]});
            var Q3;
            Q3=makeQuery(id+"F32.imprint","IMPRINT",FACE,{"disambiguationData":[TD([[makeQuery(id+"F32.imprint","IMPRINT",EDGE,{"derivedFrom":sQuery(id+"F32.wireOp",EDGE,"E41.bottom")}),-1.0]])]});
            extrude(context, id + "F33", {"entities" : qUnion([Q0, Q1, Q2, Q3]), "operationType" : NewBodyOperationType.REMOVE, "endBound" : BoundingType.THROUGH_ALL, "oppositeDirection" : true, "depth" : 25.4 * mm, "offsetDistance" : 25.4 * mm});
        }
        {
            var Q0;
            Q0=makeQuery(id+"F7.opExtrude","SWEPT_FACE",FACE,{"disambiguationData":[OSD([sQuery(id+"F6.wireOp",EDGE,"E3.left")])]});
            var sketch = newSketch(context, id + "F34", { "sketchPlane" : qUnion([Q0])});
            skLineSegment(sketch, "E43.bottom", {"start": v(6.35, 285.75) * mm, "end": v(19.05, 285.75) * mm});
            skLineSegment(sketch, "E43.top", {"start": v(6.35, 273.05) * mm, "end": v(19.05, 273.05) * mm});
            skLineSegment(sketch, "E43.left", {"start": v(6.35, 285.75) * mm, "end": v(6.35, 273.05) * mm});
            skLineSegment(sketch, "E43.right", {"start": v(19.05, 285.75) * mm, "end": v(19.05, 273.05) * mm});
            skPoint(sketch, "E43.middle", {"position": v(12.7, 279.4) * mm});
            skLineSegment(sketch, "E44.0.1.0", {"start": v(6.35, 260.35) * mm, "end": v(6.35, 247.65) * mm});
            skLineSegment(sketch, "E44.0.1.1", {"start": v(6.35, 260.35) * mm, "end": v(19.05, 260.35) * mm});
            skLineSegment(sketch, "E44.0.1.2", {"start": v(6.35, 247.65) * mm, "end": v(19.05, 247.65) * mm});
            skLineSegment(sketch, "E44.0.1.3", {"start": v(19.05, 260.35) * mm, "end": v(19.05, 247.65) * mm});
            skLineSegment(sketch, "E44.1.0.0", {"start": v(-19.05, 285.75) * mm, "end": v(-19.05, 273.05) * mm});
            skLineSegment(sketch, "E44.1.0.1", {"start": v(-19.05, 285.75) * mm, "end": v(-6.35, 285.75) * mm});
            skLineSegment(sketch, "E44.1.0.2", {"start": v(-19.05, 273.05) * mm, "end": v(-6.35, 273.05) * mm});
            skLineSegment(sketch, "E44.1.0.3", {"start": v(-6.35, 285.75) * mm, "end": v(-6.35, 273.05) * mm});
            skLineSegment(sketch, "E44.1.1.0", {"start": v(-19.05, 260.35) * mm, "end": v(-19.05, 247.65) * mm});
            skLineSegment(sketch, "E44.1.1.1", {"start": v(-19.05, 260.35) * mm, "end": v(-6.35, 260.35) * mm});
            skLineSegment(sketch, "E44.1.1.2", {"start": v(-19.05, 247.65) * mm, "end": v(-6.35, 247.65) * mm});
            skLineSegment(sketch, "E44.1.1.3", {"start": v(-6.35, 260.35) * mm, "end": v(-6.35, 247.65) * mm});
            skLineSegment(sketch, "E44.direction1", {"start": v(6.35, 273.05) * mm, "end": v(-19.05, 273.05) * mm, "construction": true});
            skLineSegment(sketch, "E44.direction2", {"start": v(6.35, 273.05) * mm, "end": v(6.35, 247.65) * mm, "construction": true});
            skSolve(sketch);
        }
        {
            var Q0;
            Q0=makeQuery(id+"F34.imprint","IMPRINT",FACE,{"disambiguationData":[TD([[makeQuery(id+"F34.imprint","IMPRINT",EDGE,{"derivedFrom":sQuery(id+"F34.wireOp",EDGE,"E44.1.0.0")}),1.0]])]});
            var Q1;
            Q1=makeQuery(id+"F34.imprint","IMPRINT",FACE,{"disambiguationData":[TD([[makeQuery(id+"F34.imprint","IMPRINT",EDGE,{"derivedFrom":sQuery(id+"F34.wireOp",EDGE,"E44.1.1.0")}),1.0]])]});
            var Q2;
            Q2=makeQuery(id+"F34.imprint","IMPRINT",FACE,{"disambiguationData":[TD([[makeQuery(id+"F34.imprint","IMPRINT",EDGE,{"derivedFrom":sQuery(id+"F34.wireOp",EDGE,"E44.0.1.0")}),1.0]])]});
            var Q3;
            Q3=makeQuery(id+"F34.imprint","IMPRINT",FACE,{"disambiguationData":[TD([[makeQuery(id+"F34.imprint","IMPRINT",EDGE,{"derivedFrom":sQuery(id+"F34.wireOp",EDGE,"E43.bottom")}),-1.0]])]});
            extrude(context, id + "F35", {"entities" : qUnion([Q0, Q1, Q2, Q3]), "operationType" : NewBodyOperationType.REMOVE, "endBound" : BoundingType.THROUGH_ALL, "oppositeDirection" : true, "depth" : 25.4 * mm, "offsetDistance" : 25.4 * mm});
        }
        {
            var Q0;
            Q0=makeQuery(id+"F9.opExtrude","CAP_FACE",FACE,{"disambiguationData":[OSD([sQuery(id+"F8.wireOp",EDGE,"E4.bottom"),sQuery(id+"F8.wireOp",EDGE,"E4.top"),sQuery(id+"F8.wireOp",EDGE,"E4.left"),sQuery(id+"F8.wireOp",EDGE,"E4.right")])],"isStart":false});
            var sketch = newSketch(context, id + "F36", { "sketchPlane" : qUnion([Q0])});
            skLineSegment(sketch, "E45.bottom", {"start": v(-6.35, 6.35) * mm, "end": v(6.35, 6.35) * mm});
            skLineSegment(sketch, "E45.top", {"start": v(-6.35, -6.35) * mm, "end": v(6.35, -6.35) * mm});
            skLineSegment(sketch, "E45.left", {"start": v(-6.35, 6.35) * mm, "end": v(-6.35, -6.35) * mm});
            skLineSegment(sketch, "E45.right", {"start": v(6.35, 6.35) * mm, "end": v(6.35, -6.35) * mm});
            skPoint(sketch, "E45.middle", {"position": v(0, 0) * mm});
            skSolve(sketch);
        }
        {
            var Q0;
            Q0 = qSketchRegion(id + "F36", true);
            extrude(context, id + "F37", {"entities" : qUnion([Q0]), "operationType" : NewBodyOperationType.REMOVE, "oppositeDirection" : true, "depth" : 25.4 * mm, "offsetDistance" : 25.4 * mm});
        }
    });
